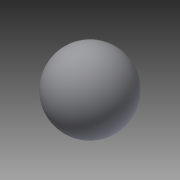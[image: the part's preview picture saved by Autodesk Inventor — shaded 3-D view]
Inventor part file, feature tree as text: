
AUTODESK INVENTOR PART (.ipt)
format: ipt  version: 2014 SP2 (Build 180246200, 246)  size: 114,176 bytes
history: native  units: mm
features: other x7, revolve x1, sketch x1
ambient origin geometry x8: Origin, YZ Plane, XZ Plane, XY Plane, X Axis, Y Axis, Z Axis, Center Point
bodies: Solid1 (feature_tree)
feature tree (9):
  revolve  "Revolution1"  [1 undecoded]
  other  "1_XY"
  other  "1_YZ"
  other  "1_ZX"
  other  "1_X"
  other  "1_Y"
  other  "1_Z"
  other  "1_Center"
  sketch  "Sketch_1"  dims[d0=360.0deg]
note: 1 required parameter value undecoded (feature->parameter linkage not recoverable at this tier; creation-order binding heuristic only, values carry confidence <= 0.55)
